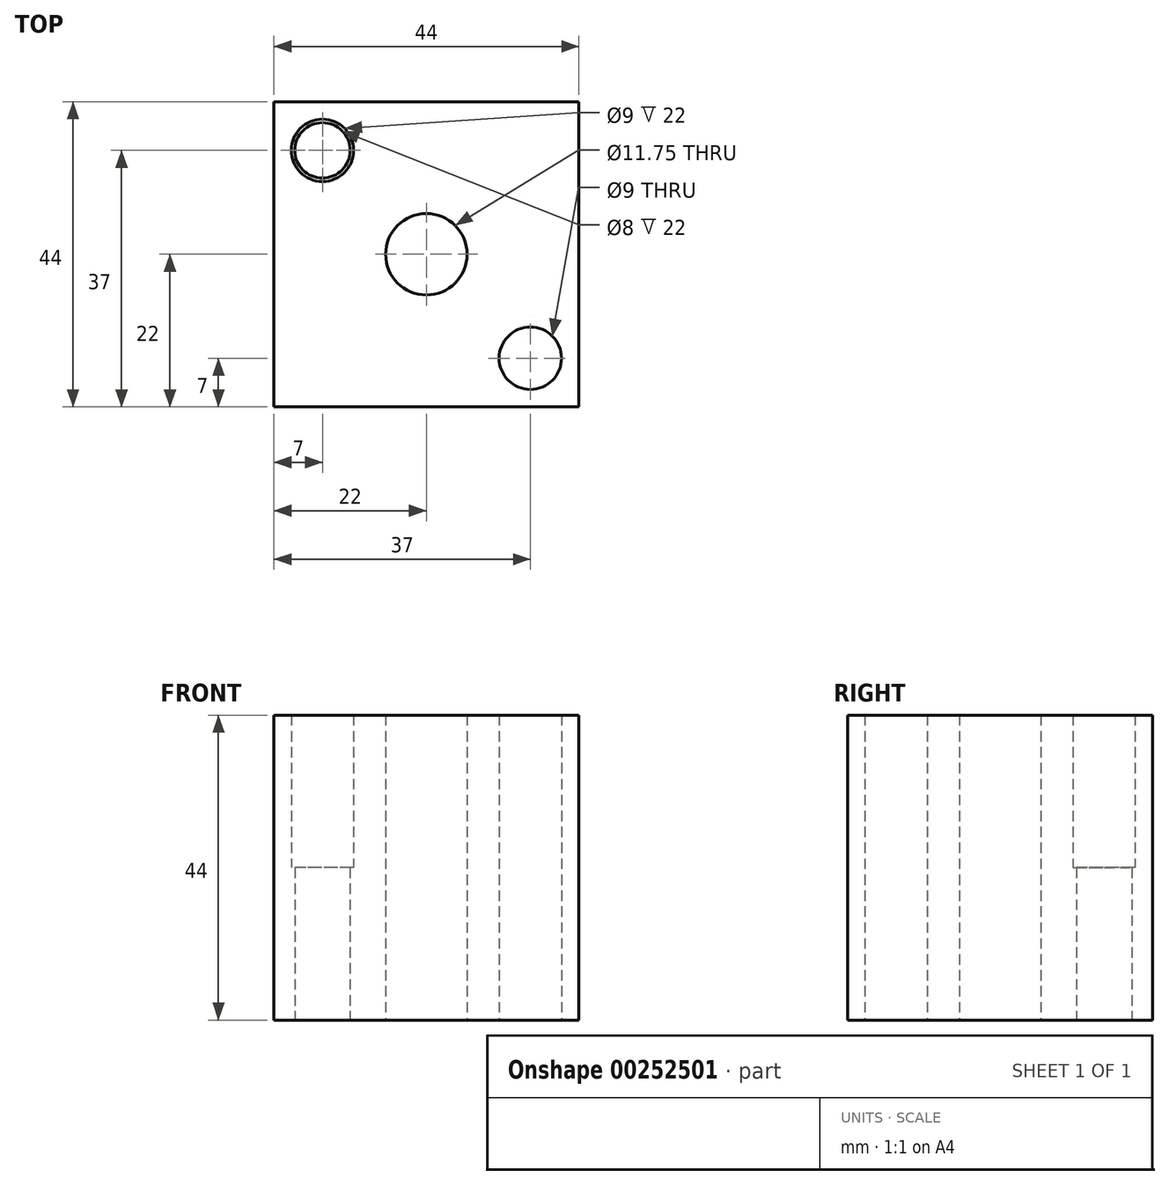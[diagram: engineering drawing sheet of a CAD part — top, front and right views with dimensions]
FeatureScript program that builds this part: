
annotation { "Feature Type Name" : "Feature", "Feature Type Description" : "" }
export const myFeature = defineFeature(function(context is Context, id is Id, definition is map)
    precondition{}
    {
        {
            var Q0;
            Q0=qCreatedBy(makeId("Top.planeOp"),FACE);
            var sketch = newSketch(context, id + "F0", { "sketchPlane" : qUnion([Q0])});
            skLineSegment(sketch, "E0.bottom", {"start": v(22, 20) * mm, "end": v(66, 20) * mm});
            skLineSegment(sketch, "E0.top", {"start": v(22, 64) * mm, "end": v(66, 64) * mm});
            skLineSegment(sketch, "E0.left", {"start": v(22, 20) * mm, "end": v(22, 64) * mm});
            skLineSegment(sketch, "E0.right", {"start": v(66, 20) * mm, "end": v(66, 64) * mm});
            skCircle(sketch, "E1", {"center": v(44, 42) * mm, "radius": 5.88 * mm});
            skPoint(sketch, "E1.centerSnap0", {"position": v(44, 64) * mm});
            skPoint(sketch, "E1.centerSnap1", {"position": v(22, 42) * mm});
            skCircle(sketch, "E2", {"center": v(29, 57) * mm, "radius": 4 * mm});
            skCircle(sketch, "E3", {"center": v(29, 57) * mm, "radius": 4.5 * mm});
            skLineSegment(sketch, "E4", {"start": v(44, 10.2) * mm, "end": v(44, 0) * mm});
            skLineSegment(sketch, "E5", {"start": v(22, 64) * mm, "end": v(66, 20) * mm, "construction": true});
            skLineSegment(sketch, "E6", {"start": v(22, 20) * mm, "end": v(66, 64) * mm, "construction": true});
            skCircle(sketch, "E7.MirrorC", {"center": v(59, 27) * mm, "radius": 4.5 * mm});
            skCircle(sketch, "E8.MirrorC", {"center": v(59, 27) * mm, "radius": 4 * mm});
            skSolve(sketch);
        }
        {
            var Q0;
            Q0=makeQuery(id+"F0.imprint","IMPRINT",FACE,{"disambiguationData":[TD([[makeQuery(id+"F0.imprint","IMPRINT",EDGE,{"derivedFrom":sQuery(id+"F0.wireOp",EDGE,"E0.bottom")}),1.0]])]});
            extrude(context, id + "F1", {"entities" : qUnion([Q0]), "depth" : 44 * mm});
        }
        {
            var Q0;
            Q0=makeQuery(id+"F0.imprint","IMPRINT",FACE,{"disambiguationData":[TD([[makeQuery(id+"F0.imprint","IMPRINT",EDGE,{"derivedFrom":sQuery(id+"F0.wireOp",EDGE,"E2")}),-1.0]])]});
            var Q1;
            Q1=makeQuery(id+"F0.imprint","IMPRINT",FACE,{"disambiguationData":[TD([[makeQuery(id+"F0.imprint","IMPRINT",EDGE,{"derivedFrom":sQuery(id+"F0.wireOp",EDGE,"E7.MirrorC")}),-1.0]])]});
            extrude(context, id + "F2", {"entities" : qUnion([Q0, Q1]), "operationType" : NewBodyOperationType.ADD, "depth" : 22 * mm});
        }
    });
